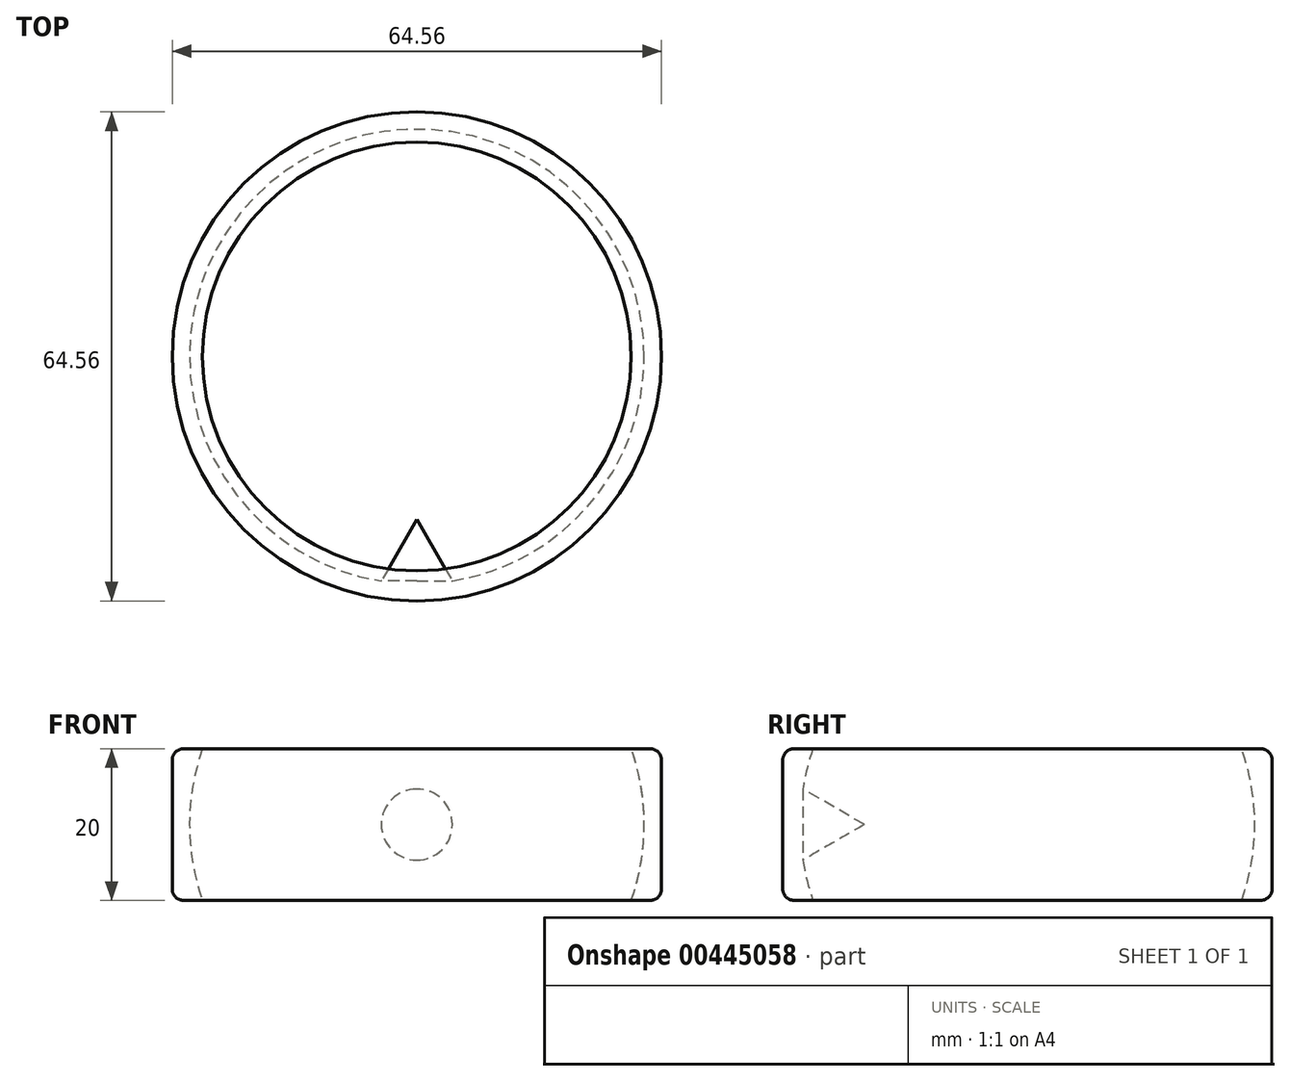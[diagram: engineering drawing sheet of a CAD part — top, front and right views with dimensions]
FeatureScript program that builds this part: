
annotation { "Feature Type Name" : "Feature", "Feature Type Description" : "" }
export const myFeature = defineFeature(function(context is Context, id is Id, definition is map)
    precondition{}
    {
        {
            var Q0;
            Q0=qCreatedBy(makeId("Front.planeOp"),FACE);
            var sketch = newSketch(context, id + "F0", { "sketchPlane" : qUnion([Q0])});
            skArc(sketch, "E0", {"start": v(28.28, 10) * mm, "mid": v(30, 0) * mm, "end": v(28.28, -10) * mm});
            skLineSegment(sketch, "E1", {"start": v(28.28, 10) * mm, "end": v(32.28, 10) * mm});
            skLineSegment(sketch, "E2", {"start": v(28.28, -10) * mm, "end": v(32.28, -10) * mm});
            skLineSegment(sketch, "E3", {"start": v(32.28, 10) * mm, "end": v(32.28, -10) * mm});
            skPoint(sketch, "E4", {"position": v(32.28, 0) * mm});
            skLineSegment(sketch, "E5", {"start": v(0, 5.08) * mm, "end": v(0, -5.1) * mm});
            skSolve(sketch);
        }
        {
            var Q0;
            Q0 = qSketchRegion(id + "F0", true);
            var Q1;
            Q1=sQuery(id+"F0.wireOp",EDGE,"E5");
            revolve(context, id + "F1", {"entities" : qUnion([Q0]), "axis" : qUnion([Q1]), "revolveType" : RevolveType.FULL});
        }
        {
            var Q0;
            Q0=qCreatedBy(makeId("Right.planeOp"),FACE);
            var sketch = newSketch(context, id + "F2", { "sketchPlane" : qUnion([Q0])});
            skLineSegment(sketch, "E6", {"start": v(-34.5, 7.5) * mm, "end": v(-34.5, -7.5) * mm});
            skLineSegment(sketch, "E7", {"start": v(-34.5, -7.5) * mm, "end": v(-21.5, 0) * mm});
            skLineSegment(sketch, "E8", {"start": v(-21.5, 0) * mm, "end": v(-34.5, 7.5) * mm});
            skLineSegment(sketch, "E9", {"start": v(-21.5, 0) * mm, "end": v(-34.5, 0) * mm});
            skSolve(sketch);
        }
        {
            var Q0;
            {var subQ0=sQuery(id+"F2.wireOp",EDGE,"E8");Q0=makeQuery(id+"F2.imprint","IMPRINT",FACE,{"disambiguationData":[TD([[makeQuery(id+"F2.imprint","IMPRINT",EDGE,{"derivedFrom":subQ0}),1.0]])]});}
            var Q1;
            Q1=sQuery(id+"F2.wireOp",EDGE,"E9");
            revolve(context, id + "F3", {"operationType" : NewBodyOperationType.ADD, "entities" : qUnion([Q0]), "axis" : qUnion([Q1]), "revolveType" : RevolveType.FULL});
        }
        {
            var Q0;
            Q0=qCreatedBy(makeId("Top.planeOp"),FACE);
            var sketch = newSketch(context, id + "F4", { "sketchPlane" : qUnion([Q0])});
            skCircle(sketch, "E10.0", {"center": v(0, 0) * mm, "radius": 32.28 * mm});
            skCircle(sketch, "E11.0", {"center": v(0, 0) * mm, "radius": 37.28 * mm});
            skSolve(sketch);
        }
        {
            var Q0;
            Q0 = qSketchRegion(id + "F4", true);
            extrude(context, id + "F5", {"entities" : qUnion([Q0]), "operationType" : NewBodyOperationType.REMOVE, "endBound" : BoundingType.SYMMETRIC, "oppositeDirection" : true, "depth" : 25 * mm});
        }
        {
            var Q0;
            Q0=makeQuery(id+"F1.opRevolve","SWEPT_EDGE",EDGE,{"disambiguationData":[OSD([sQuery(id+"F0.wireOp",EDGE,"E1"),sQuery(id+"F0.wireOp",EDGE,"E3")])]});
            var Q1;
            Q1=makeQuery(id+"F1.opRevolve","SWEPT_EDGE",EDGE,{"disambiguationData":[OSD([sQuery(id+"F0.wireOp",EDGE,"E2"),sQuery(id+"F0.wireOp",EDGE,"E3")])]});
            var Q2;
            Q2=makeQuery(id+"F1rQ6Lwv2hyK4NG_1.opExtrude","CAP_EDGE",EDGE,{"disambiguationData":[OSD([sQuery(id+"FxohBJ6Nne7WmOy_1.wireOp",EDGE,"P5x6Lbt4-V0H8-2KIa-tIWg-1hcAFY5jkGy4")])],"isStart":false});
            var Q3;
            Q3=makeQuery(id+"F1rQ6Lwv2hyK4NG_1.opExtrude","CAP_EDGE",EDGE,{"disambiguationData":[OSD([sQuery(id+"FxohBJ6Nne7WmOy_1.wireOp",EDGE,"P5x6Lbt4-V0H8-2KIa-tIWg-1hcAFY5jkGy4")])],"isStart":true});
            var Q4;
            Q4=makeQuery(id+"FUOA13UBdlQfGhi_1.boolean.opBoolean","COPY",FACE,{"derivedFrom":makeQuery(id+"FUOA13UBdlQfGhi_1.opExtrude","SWEPT_FACE",FACE,{"disambiguationData":[OSD([sQuery(id+"FuAagUdgKmEIQYZ_1.wireOp",EDGE,"euqjfqfg-1YUr-tmrH-6KyW-pai8Kwf5nV6q")])]})});
            fillet(context, id + "F6", {"entities" : qUnion([Q0, Q1, Q2, Q3, Q4]), "radius" : 1.5 * mm, "tangentPropagation" : true, "allowEdgeOverflow" : false});
        }
    });
